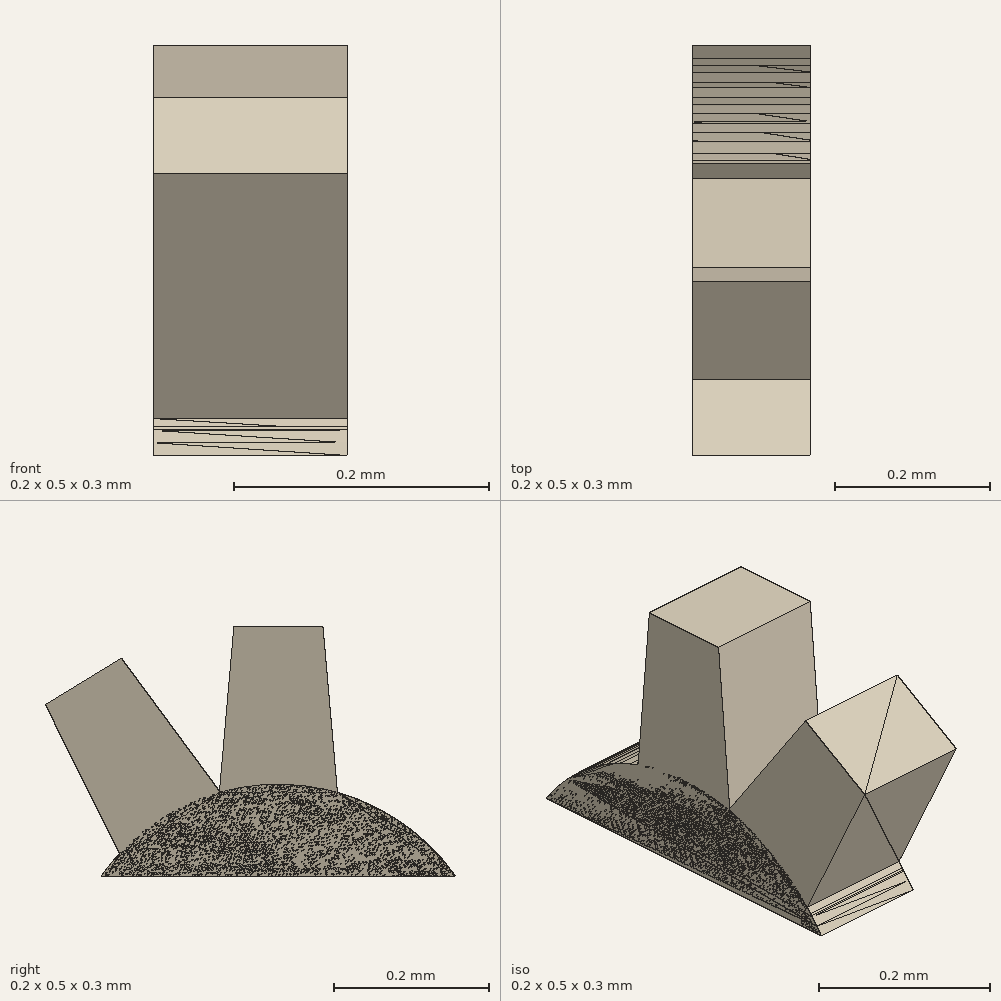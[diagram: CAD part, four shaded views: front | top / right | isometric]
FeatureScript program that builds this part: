
annotation { "Feature Type Name" : "Feature", "Feature Type Description" : "" }
export const myFeature = defineFeature(function(context is Context, id is Id, definition is map)
    precondition{}
    {
        {
            var Q0;
            Q0=qCreatedBy(makeId("Right.planeOp"),FACE);
            var sketch = newSketch(context, id + "F0", { "sketchPlane" : qUnion([Q0])});
            skLineSegment(sketch, "E0.bottom", {"start": v(-0.23, 0.08) * mm, "end": v(0.23, 0.08) * mm, "construction": true});
            skLineSegment(sketch, "E0.top", {"start": v(-0.23, 0) * mm, "end": v(0.23, 0) * mm});
            skLineSegment(sketch, "E0.left", {"start": v(-0.23, 0.08) * mm, "end": v(-0.23, 0) * mm, "construction": true});
            skLineSegment(sketch, "E0.right", {"start": v(0.23, 0.08) * mm, "end": v(0.23, 0) * mm, "construction": true});
            skArc(sketch, "E1", {"start": v(0.23, 0) * mm, "mid": v(0, 0.12) * mm, "end": v(-0.23, 0) * mm});
            skLineSegment(sketch, "E2", {"start": v(0, -0.16) * mm, "end": v(0, 0.32) * mm, "construction": true});
            skLineSegment(sketch, "E3", {"start": v(-0.08, 0.1) * mm, "end": v(-0.06, 0.32) * mm});
            skLineSegment(sketch, "E4", {"start": v(-0.06, 0.32) * mm, "end": v(0, 0.32) * mm});
            skLineSegment(sketch, "E5.MirrorCS", {"start": v(0.06, 0.32) * mm, "end": v(0, 0.32) * mm});
            skLineSegment(sketch, "E6.MirrorCS", {"start": v(0.08, 0.1) * mm, "end": v(0.06, 0.32) * mm});
            skSolve(sketch);
        }
        {
            var Q0;
            {var subQ0=sQuery(id+"F0.wireOp",EDGE,"E0.top");Q0=makeQuery(id+"F0.imprint","IMPRINT",FACE,{"disambiguationData":[TD([[makeQuery(id+"F0.imprint","IMPRINT",EDGE,{"derivedFrom":subQ0}),1.0]])]});}
            var Q1;
            {var subQ0=sQuery(id+"F0.wireOp",EDGE,"E3");Q1=makeQuery(id+"F0.imprint","IMPRINT",FACE,{"disambiguationData":[TD([[makeQuery(id+"F0.imprint","IMPRINT",EDGE,{"derivedFrom":subQ0}),-1.0]])]});}
            extrude(context, id + "F1", {"entities" : qUnion([Q0, Q1]), "endBound" : BoundingType.SYMMETRIC, "depth" : 0.15 * mm});
        }
        {
            var Q0;
            Q0=qCreatedBy(makeId("Right.planeOp"),FACE);
            var sketch = newSketch(context, id + "F2", { "sketchPlane" : qUnion([Q0])});
            skArc(sketch, "E7.0", {"start": v(0.23, 0) * mm, "mid": v(0, 0.12) * mm, "end": v(-0.23, 0) * mm});
            skLineSegment(sketch, "E8.0", {"start": v(-0.23, 0) * mm, "end": v(0.23, 0) * mm});
            skLineSegment(sketch, "E9", {"start": v(0, -0.16) * mm, "end": v(-0.25, 0.25) * mm, "construction": true});
            skLineSegment(sketch, "E10", {"start": v(-0.2, 0.03) * mm, "end": v(-0.3, 0.22) * mm});
            skLineSegment(sketch, "E11", {"start": v(-0.3, 0.22) * mm, "end": v(-0.25, 0.25) * mm});
            skLineSegment(sketch, "E12.MirrorCS", {"start": v(-0.2, 0.28) * mm, "end": v(-0.25, 0.25) * mm});
            skLineSegment(sketch, "E13.MirrorCS", {"start": v(-0.08, 0.1) * mm, "end": v(-0.2, 0.28) * mm});
            skSolve(sketch);
        }
        {
            var Q0;
            {var subQ0=sQuery(id+"F2.wireOp",EDGE,"E10");Q0=makeQuery(id+"F2.imprint","IMPRINT",FACE,{"disambiguationData":[TD([[makeQuery(id+"F2.imprint","IMPRINT",EDGE,{"derivedFrom":subQ0}),-1.0]])]});}
            var Q1;
            {var subQ0=sQuery(id+"F2.wireOp",EDGE,"E8.0");Q1=makeQuery(id+"F2.imprint","IMPRINT",FACE,{"disambiguationData":[TD([[makeQuery(id+"F2.imprint","IMPRINT",EDGE,{"derivedFrom":subQ0}),1.0]])]});}
            extrude(context, id + "F3", {"entities" : qUnion([Q0, Q1]), "endBound" : BoundingType.SYMMETRIC, "depth" : 0.15 * mm});
        }
        {
            var Q0;
            Q0=makeQuery(id+"F3.opExtrude","SWEPT_BODY",BODY,{"disambiguationData":[OSD([sQuery(id+"F2.wireOp",EDGE,"E7.0"),sQuery(id+"F2.wireOp",EDGE,"E8.0"),sQuery(id+"F2.wireOp",EDGE,"E10"),sQuery(id+"F2.wireOp",EDGE,"E11"),sQuery(id+"F2.wireOp",EDGE,"E12.MirrorCS"),sQuery(id+"F2.wireOp",EDGE,"E13.MirrorCS")])]});
            transform(context, id + "F4", {"entities" : qUnion([Q0]), "transformType" : TransformType.COPY});
        }
    });
